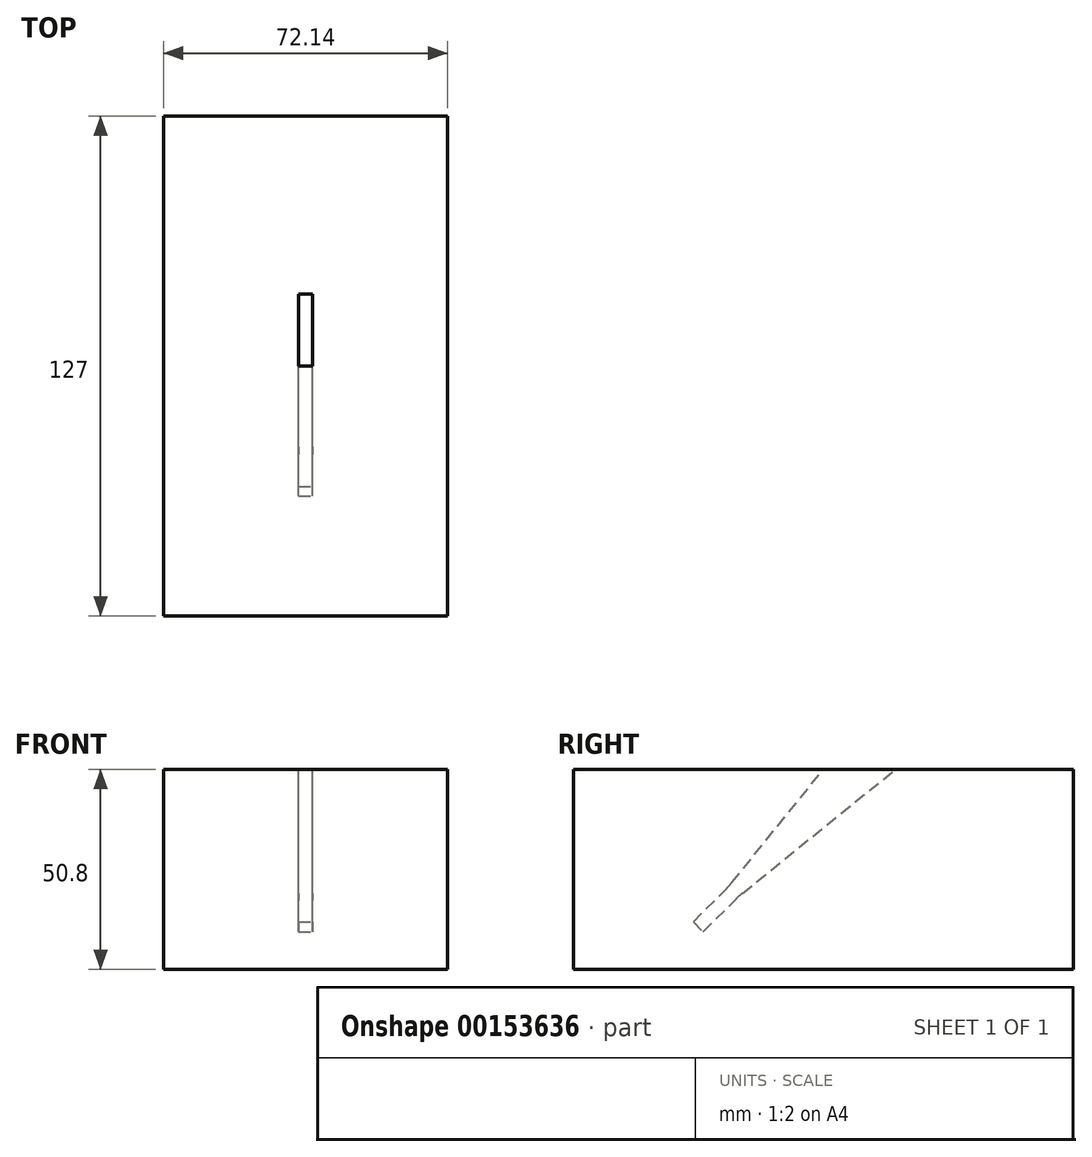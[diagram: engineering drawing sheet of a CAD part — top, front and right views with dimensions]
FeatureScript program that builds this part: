
annotation { "Feature Type Name" : "Feature", "Feature Type Description" : "" }
export const myFeature = defineFeature(function(context is Context, id is Id, definition is map)
    precondition{}
    {
        {
            var Q0;
            Q0=qCreatedBy(makeId("Right.planeOp"),FACE);
            var sketch = newSketch(context, id + "F0", { "sketchPlane" : qUnion([Q0])});
            skLineSegment(sketch, "E0", {"start": v(-33.07, -38.73) * mm, "end": v(-25.03, -30.7) * mm});
            skLineSegment(sketch, "E1.bottom", {"start": v(-63.5, 0) * mm, "end": v(0, 0) * mm});
            skLineSegment(sketch, "E1.top", {"start": v(-63.5, -50.8) * mm, "end": v(63.5, -50.8) * mm});
            skLineSegment(sketch, "E1.left", {"start": v(-63.5, 0) * mm, "end": v(-63.5, -50.8) * mm});
            skLineSegment(sketch, "E1.right", {"start": v(63.5, 0) * mm, "end": v(63.5, -50.8) * mm});
            skLineSegment(sketch, "E2", {"start": v(0, 13.72) * mm, "end": v(0, -28.63) * mm, "construction": true});
            skLineSegment(sketch, "E3", {"start": v(-18.84, -27.02) * mm, "end": v(16.94, 8.76) * mm, "construction": true});
            skLineSegment(sketch, "E4", {"start": v(-23.26, -28.72) * mm, "end": v(0, 0) * mm});
            skLineSegment(sketch, "E5.MirrorCS", {"start": v(-20.54, -31.43) * mm, "end": v(18.27, 0) * mm});
            skLineSegment(sketch, "E6.MirrorCS", {"start": v(-30.56, -41.25) * mm, "end": v(-22.52, -33.2) * mm});
            skLineSegment(sketch, "E7", {"start": v(-33.07, -38.73) * mm, "end": v(-30.56, -41.25) * mm});
            skPoint(sketch, "E8.visualSharp", {"position": v(-24.1, -29.75) * mm});
            skArc(sketch, "E8.filletArc", {"start": v(-25.03, -30.7) * mm, "mid": v(-24.12, -29.73) * mm, "end": v(-23.26, -28.72) * mm});
            skPoint(sketch, "E9.visualSharp", {"position": v(-21.58, -32.27) * mm});
            skArc(sketch, "E9.filletArc", {"start": v(-20.54, -31.43) * mm, "mid": v(-21.56, -32.3) * mm, "end": v(-22.52, -33.2) * mm});
            skLineSegment(sketch, "E10", {"start": v(0, 0) * mm, "end": v(8.17, -8.17) * mm});
            skPoint(sketch, "E11.visualSharp", {"position": v(0, 0) * mm});
            skLineSegment(sketch, "E12", {"start": v(18.27, 0) * mm, "end": v(63.5, 0) * mm});
            skLineSegment(sketch, "E13", {"start": v(0, 0) * mm, "end": v(18.27, 0) * mm});
            skSolve(sketch);
        }
        {
            var Q0;
            Q0=qSketchRegion(id+"F0",true);
            var Q1;
            Q1=makeQuery(id+"F0.imprint","IMPRINT",FACE,{"disambiguationData":[TD([[makeQuery(id+"F0.imprint","IMPRINT",EDGE,{"derivedFrom":sQuery(id+"F0.wireOp",EDGE,"E0")}),1.0]])]});
            extrude(context, id + "F1", {"entities" : qUnion([Q0, Q1]), "endBound" : BoundingType.SYMMETRIC, "depth" : 72.14 * mm});
        }
        {
            var Q0;
            Q0=makeQuery(id+"F0.imprint","IMPRINT",FACE,{"disambiguationData":[TD([[makeQuery(id+"F0.imprint","IMPRINT",EDGE,{"derivedFrom":sQuery(id+"F0.wireOp",EDGE,"E0")}),-1.0]])]});
            var Q1;
            {var subQ2=sQuery(id+"F0.wireOp",EDGE,"E10");Q1=makeQuery(id+"F0.imprint","IMPRINT",FACE,{"disambiguationData":[TD([[makeQuery(id+"F0.imprint","IMPRINT",EDGE,{"derivedFrom":subQ2}),1.0]])]});}
            extrude(context, id + "F2", {"entities" : qUnion([Q0, Q1]), "operationType" : NewBodyOperationType.REMOVE, "endBound" : BoundingType.SYMMETRIC, "oppositeDirection" : true, "depth" : 3.54 * mm});
        }
    });
